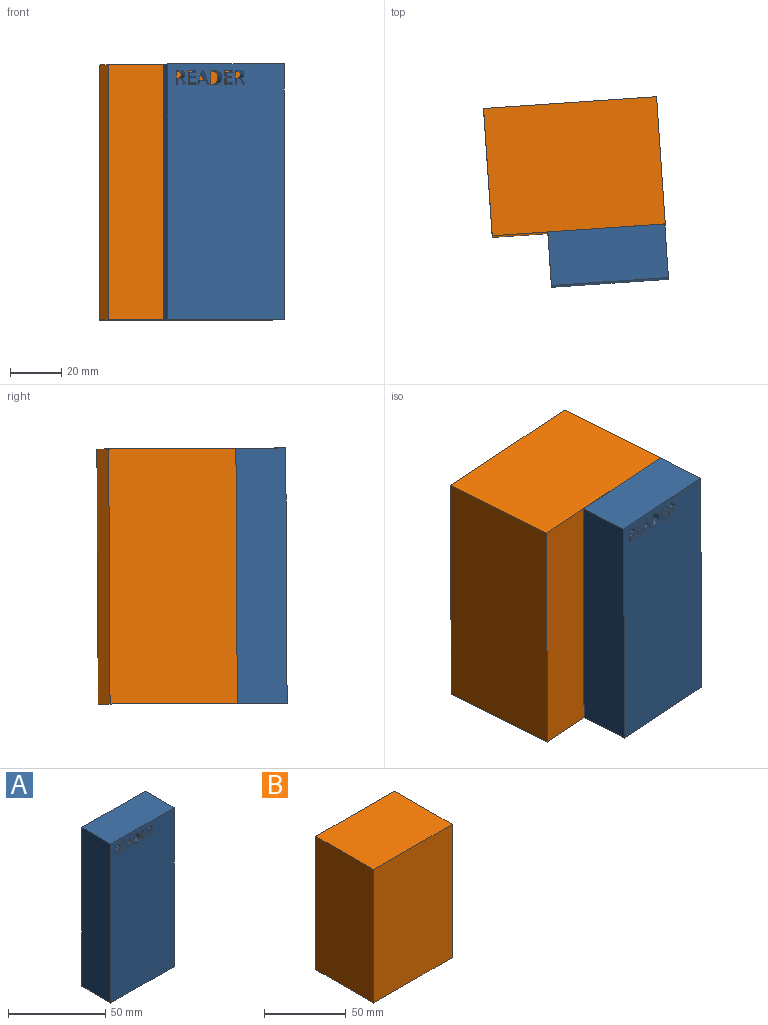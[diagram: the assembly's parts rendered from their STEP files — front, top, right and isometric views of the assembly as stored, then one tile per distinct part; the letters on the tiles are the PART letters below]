
ASSEMBLY  parts=2 mates=1
PART A: 67 faces, bbox 46x21.1x100.1 mm
  f0: plane 45.97x21.08mm, normal (0,0,1), area 969.2mm2, adj f1,f64,f65,f66
  f1: plane 100.08x21.08mm, normal (-1,0,0), area 2109.8mm2, adj f0,f2,f65,f66
  f2: plane 45.97x21.08mm, normal (0,0,-1), area 969.2mm2, adj f1,f64,f65,f66
  f3: plane 21.08x0.56mm, normal (-1,0,0), area 11.7mm2, adj f4,f58,f65,f66
  f4: plane 21.08x2.99mm, normal (0,0,1), area 63mm2, adj f3,f5,f65,f66
  f5: plane 21.08x5.36mm, normal (1,0,0), area 113mm2, adj f4,f6,f65,f66
  f6: plane 21.08x2.99mm, normal (0,0,-1), area 63mm2, adj f5,f7,f65,f66
  f7: plane 21.08x0.55mm, normal (-1,0,0), area 11.7mm2, adj f6,f8,f65,f66
  f8: plane 21.08x2.37mm, normal (0,0,1), area 49.9mm2, adj f7,f9,f65,f66
  f9: plane 21.08x1.73mm, normal (-1,0,0), area 36.4mm2, adj f8,f10,f65,f66
  f10: plane 21.08x2.22mm, normal (0,0,-1), area 46.8mm2, adj f9,f11,f65,f66
  f11: plane 21.08x0.55mm, normal (-1,0,0), area 11.6mm2, adj f10,f12,f65,f66
  f12: plane 21.08x2.22mm, normal (0,0,1), area 46.8mm2, adj f11,f13,f65,f66
  f13: plane 21.08x1.97mm, normal (-1,0,0), area 41.6mm2, adj f12,f58,f65,f66
  f14: plane 21.08x0.65mm, normal (0,0,1), area 13.6mm2, adj f15,f59,f65,f66
  f15: plane 21.08x1.7mm, normal (0.93,0,0.36), area 38.6mm2, adj f14,f16,f65,f66
  f16: plane 21.08x2.15mm, normal (0,0,1), area 45.3mm2, adj f15,f17,f65,f66
  f17: plane 21.08x1.7mm, normal (-0.93,0,0.36), area 38.5mm2, adj f16,f18,f65,f66
  f18: plane 21.08x0.63mm, normal (0,0,1), area 13.3mm2, adj f17,f19,f65,f66
  f19: plane 21.08x5.38mm, normal (0.93,0,-0.37), area 122mm2, adj f18,f20,f65,f66
  f20: plane 21.08x0.52mm, normal (0,0,-1), area 11.1mm2, adj f19,f59,f65,f66
  f21: plane 21.08x0.56mm, normal (-1,0,0), area 11.7mm2, adj f22,f60,f65,f66
  f22: plane 21.08x2.99mm, normal (0,0,1), area 63mm2, adj f21,f23,f65,f66
  f23: plane 21.08x5.36mm, normal (1,0,0), area 113mm2, adj f22,f24,f65,f66
  f24: plane 21.08x2.99mm, normal (0,0,-1), area 63mm2, adj f23,f25,f65,f66
  f25: plane 21.08x0.55mm, normal (-1,0,0), area 11.7mm2, adj f24,f26,f65,f66
  f26: plane 21.08x2.37mm, normal (0,0,1), area 49.9mm2, adj f25,f27,f65,f66
  f27: plane 21.08x1.73mm, normal (-1,0,0), area 36.4mm2, adj f26,f28,f65,f66
  f28: plane 21.08x2.22mm, normal (0,0,-1), area 46.8mm2, adj f27,f29,f65,f66
  f29: plane 21.08x0.55mm, normal (-1,0,0), area 11.6mm2, adj f28,f30,f65,f66
  f30: plane 21.08x2.22mm, normal (0,0,1), area 46.8mm2, adj f29,f31,f65,f66
  f31: plane 21.08x1.97mm, normal (-1,0,0), area 41.6mm2, adj f30,f60,f65,f66
  f32: plane 21.08x1.12mm, normal (0,0,1), area 23.6mm2, adj f33,f61,f65,f66
  f33: plane 21.08x2.23mm, normal (-1,0,0), area 47mm2, adj f32,f34,f65,f66
  f34: plane 21.08x0.62mm, normal (0,0,1), area 13.1mm2, adj f33,f35,f65,f66
  f35: plane 21.08x5.36mm, normal (1,0,0), area 113mm2, adj f34,f36,f65,f66
  f36: plane 21.08x1.47mm, normal (0,0,-1), area 31mm2, adj f35,f37,f65,f66
  f37: extruded ~21.08x1.46mm, area 32.3mm2, adj f36,f38,f65,f66
  f38: extruded ~21.08x1.14mm, area 26.9mm2, adj f37,f39,f65,f66
  f39: extruded ~21.08x1.44mm, area 40.9mm2, adj f38,f40,f65,f66
  f40: plane 21.08x2.41mm, normal (-0.86,0,-0.52), area 59.3mm2, adj f39,f41,f65,f66
  f41: plane 21.08x0.74mm, normal (0,0,1), area 15.5mm2, adj f40,f61,f65,f66
  f42: extruded ~21.08x1.94mm, area 44.5mm2, adj f43,f62,f65,f66
  f43: extruded ~21.08x2.03mm, area 46.7mm2, adj f42,f44,f65,f66
  f44: extruded ~21.08x2.07mm, area 47.3mm2, adj f43,f45,f65,f66
  f45: plane 21.08x1.49mm, normal (0,0,1), area 31.3mm2, adj f44,f46,f65,f66
  f46: plane 21.08x5.36mm, normal (1,0,0), area 113mm2, adj f45,f47,f65,f66
  f47: plane 21.08x1.64mm, normal (0,0,-1), area 34.6mm2, adj f46,f62,f65,f66
  f48: plane 21.08x1.12mm, normal (0,0,1), area 23.6mm2, adj f49,f63,f65,f66
  f49: plane 21.08x2.23mm, normal (-1,0,0), area 47mm2, adj f48,f50,f65,f66
  f50: plane 21.08x0.62mm, normal (0,0,1), area 13.1mm2, adj f49,f51,f65,f66
  f51: plane 21.08x5.36mm, normal (1,0,0), area 113mm2, adj f50,f52,f65,f66
  f52: plane 21.08x1.47mm, normal (0,0,-1), area 31mm2, adj f51,f53,f65,f66
  f53: extruded ~21.08x1.46mm, area 32.3mm2, adj f52,f54,f65,f66
  f54: extruded ~21.08x1.14mm, area 26.9mm2, adj f53,f55,f65,f66
  f55: extruded ~21.08x1.44mm, area 40.9mm2, adj f54,f56,f65,f66
  f56: plane 21.08x2.41mm, normal (-0.86,0,-0.52), area 59.3mm2, adj f55,f57,f65,f66
  f57: plane 21.08x0.74mm, normal (0,0,1), area 15.5mm2, adj f56,f63,f65,f66
  f58: plane 21.08x2.37mm, normal (0,0,-1), area 49.9mm2, adj f3,f13,f65,f66
  f59: plane 21.08x5.38mm, normal (-0.93,0,-0.36), area 121.9mm2, adj f14,f20,f65,f66
  f60: plane 21.08x2.37mm, normal (0,0,-1), area 49.9mm2, adj f21,f31,f65,f66
  f61: plane 21.08x2.23mm, normal (0.86,0,0.5), area 54.4mm2, adj f32,f41,f65,f66
  f62: extruded ~21.08x1.94mm, area 44.7mm2, adj f42,f47,f65,f66
  f63: plane 21.08x2.23mm, normal (0.86,0,0.5), area 54.4mm2, adj f48,f57,f65,f66
  f64: plane 100.08x21.08mm, normal (1,0,0), area 2109.8mm2, adj f0,f2,f65,f66
  f65: plane 100.08x45.97mm, normal (0,-1,0), area 4531.6mm2, adj f0,f1,f2,f3,f4,f5,f6,f7
  f66: plane 100.08x45.97mm, normal (0,1,0), area 4531.6mm2, adj f0,f1,f2,f3,f4,f5,f6,f7
PART B: 6 faces, bbox 68x50x100 mm
  f0: plane 68x50mm, normal (0,0,1), area 3400mm2, adj f1,f3,f4,f5
  f1: plane 100x50mm, normal (-1,0,0), area 5000mm2, adj f0,f2,f4,f5
  f2: plane 68x50mm, normal (0,0,-1), area 3400mm2, adj f1,f3,f4,f5
  f3: plane 100x50mm, normal (1,0,0), area 5000mm2, adj f0,f2,f4,f5
  f4: plane 100x68mm, normal (0,-1,0), area 6800mm2, adj f0,f1,f2,f3
  f5: plane 100x68mm, normal (0,1,0), area 6800mm2, adj f0,f1,f2,f3
PLACE A rot(axis=(-0.08,0,1),3.9deg) t=(-0.22,-24.38,0.79)mm
PLACE B rot(axis=(-0.08,0,1),3.9deg) t=(-14.43,24.76,0.53)mm
MATE planar A.f66 <-> B.f4  axis (-0.07,1,-0.01) through (-0.12,-24.38,0.11)mm
